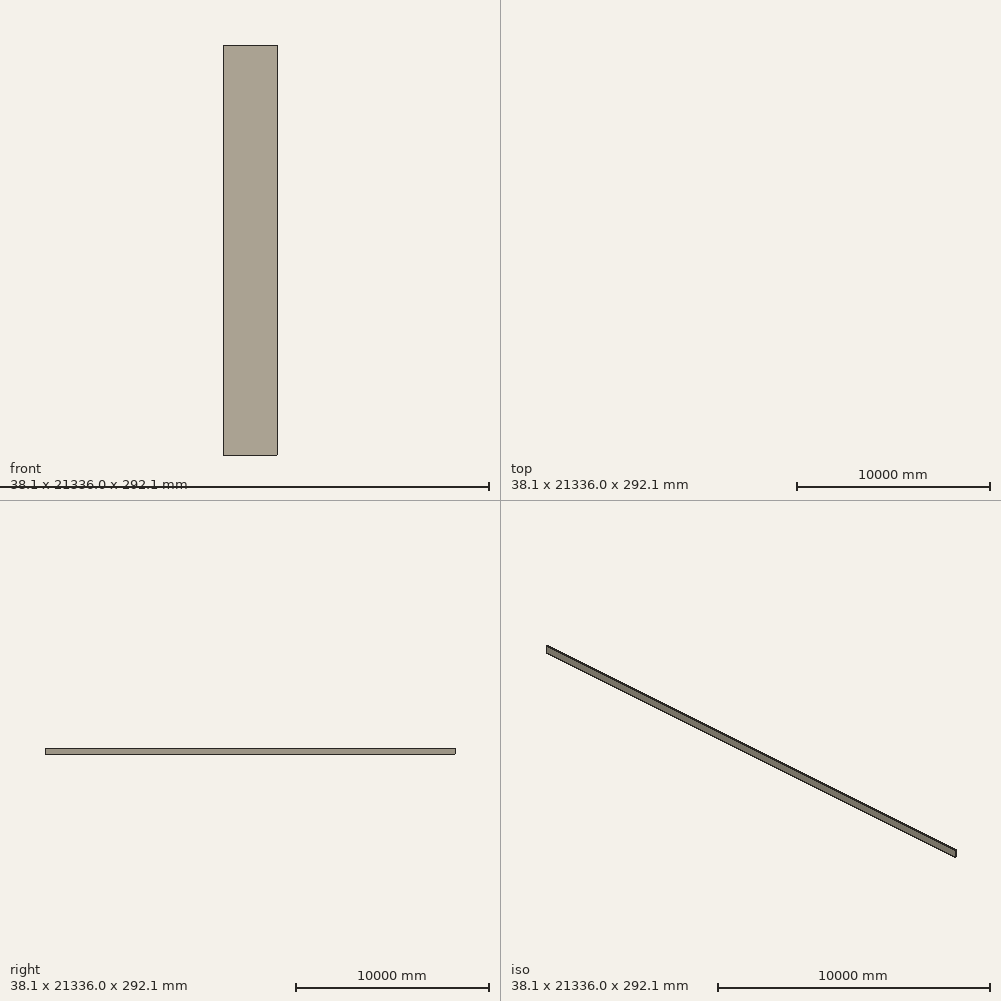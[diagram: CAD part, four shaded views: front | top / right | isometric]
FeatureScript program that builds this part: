
annotation { "Feature Type Name" : "Feature", "Feature Type Description" : "" }
export const myFeature = defineFeature(function(context is Context, id is Id, definition is map)
    precondition{}
    {
        {
            var Q0;
            Q0=qCreatedBy(makeId("Front.planeOp"),FACE);
            var sketch = newSketch(context, id + "F0", { "sketchPlane" : qUnion([Q0])});
            skLineSegment(sketch, "E0.bottom", {"start": v(0, 0) * mm, "end": v(38.1, 0) * mm});
            skLineSegment(sketch, "E0.top", {"start": v(0, 292.1) * mm, "end": v(38.1, 292.1) * mm});
            skLineSegment(sketch, "E0.left", {"start": v(0, 0) * mm, "end": v(0, 292.1) * mm});
            skLineSegment(sketch, "E0.right", {"start": v(38.1, 0) * mm, "end": v(38.1, 292.1) * mm});
            skSolve(sketch);
        }
        {
            var Q0;
            Q0 = qSketchRegion(id + "F0", true);
            extrude(context, id + "F1", {"entities" : qUnion([Q0]), "depth" : 21336 * mm});
        }
    });
